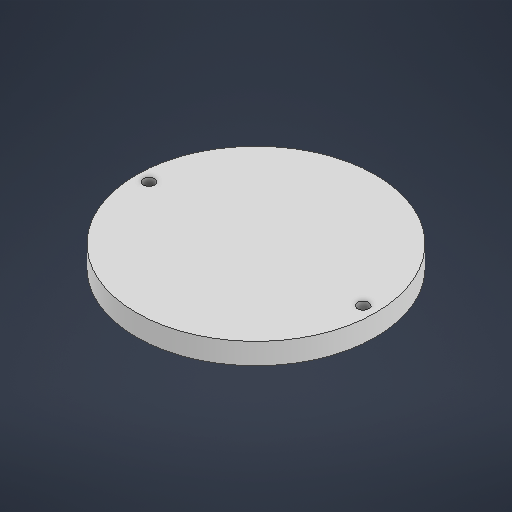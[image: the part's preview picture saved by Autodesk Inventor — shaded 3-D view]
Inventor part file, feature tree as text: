
AUTODESK INVENTOR PART (.ipt)
format: ipt  version: 2025 (Build 290162000, 162)  size: 235,520 bytes
history: native  units: in
note: dims shown in document units (in); Inventor stores cm internally (conversion verified against a paired STEP export)
features: sketch x4, extrude x3, hole x2
ambient origin geometry x8: Origin, YZ Plane, XZ Plane, XY Plane, X Axis, Y Axis, Z Axis, Center Point
bodies: Solid1 (feature_tree)
feature tree (9):
  extrude  "Extrusion1"  Depth=0.5906in TaperAngle=0.0deg
  sketch  "Sketch2"  dims[d3=5.9843in d4=0.315in]
  extrude  "Extrusion2"  Depth=0.315in
  extrude  "Extrusion3"  Depth=0.1772in
  hole  "Hole1"  [1 undecoded]
  hole  "Hole2"  [1 undecoded]
  sketch  "Sketch1"  dims[d0=6.6732in d1=0.5906in d2=0.0in]
  sketch  "Sketch3"  dims[d5=0.315in d6=0.1772in]
  sketch  "Sketch4"  dims[d7=0.1772in d8=0.0in d9=0.0in d10=0.4724in d11=0.0in d12=0.3979in d13=0.4724in d14=0.4409in d15=0.0787in d16=90.0deg d17=0.4724in d18=0.0in d19=4.3307in d20=0.315in d21=0.315in d22=0.315in d23=0.315in d24=0.2617in d25=0.4724in d26=0.1575in d27=0.0787in d28=90.0deg d29=0.4724in d30=0.0in]
note: 2 required parameter values undecoded (feature->parameter linkage not recoverable at this tier; creation-order binding heuristic only, values carry confidence <= 0.55)
